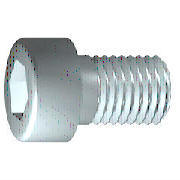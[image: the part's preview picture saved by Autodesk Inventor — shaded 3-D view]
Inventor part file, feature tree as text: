
AUTODESK INVENTOR PART (.ipt)
format: ipt  version: 2017 (Build 210142000, 142)  size: 190,464 bytes
history: native  units: mm (DEFAULTED — no unit token found)
features: sketch x2, other x1, extrude x1, plane x1, fillet x1
ambient origin geometry x7: Origin, YZ Plane, XY Plane, X Axis, Y Axis, Z Axis, Center Point
bodies: Solid1 (feature_tree)
feature tree (6):
  other  "Corps"
  extrude  "Rainure"  Depth=10.75mm
  plane  "Work Plane1"
  fillet  "Fillet2"  Radius=0.306825mm
  sketch  "Esquisse1"
  sketch  "Esquisse2"
